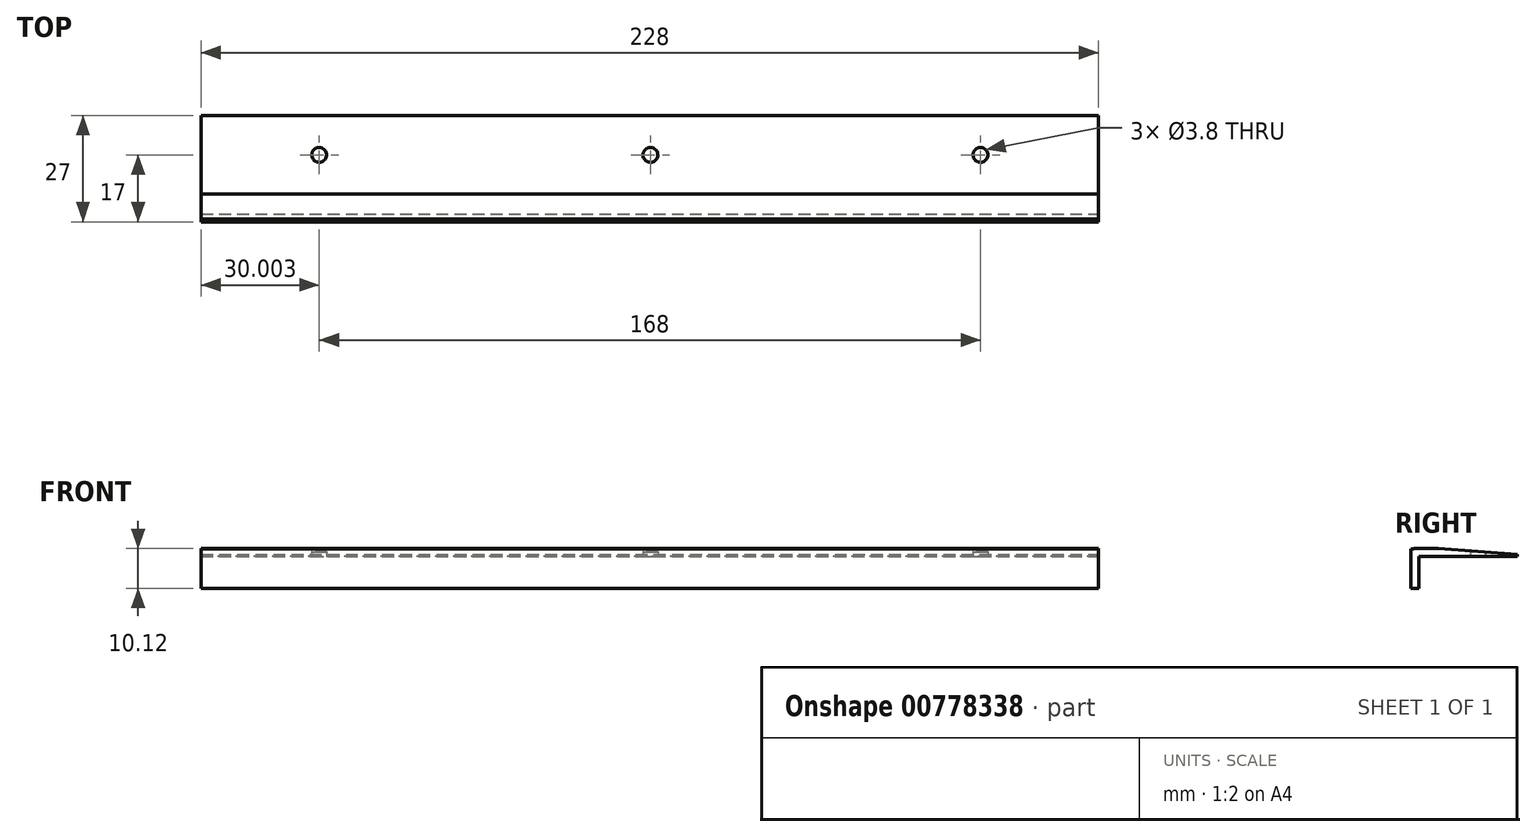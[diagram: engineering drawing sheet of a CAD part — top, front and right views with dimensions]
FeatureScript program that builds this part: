
annotation { "Feature Type Name" : "Feature", "Feature Type Description" : "" }
export const myFeature = defineFeature(function(context is Context, id is Id, definition is map)
    precondition{}
    {
        {
            var Q0;
            Q0=qCreatedBy(makeId("Front.planeOp"),FACE);
            var sketch = newSketch(context, id + "F0", { "sketchPlane" : qUnion([Q0])});
            skLineSegment(sketch, "E0.bottom", {"start": v(-110.8, 18.46) * mm, "end": v(117.2, 18.46) * mm});
            skLineSegment(sketch, "E0.top", {"start": v(-110.8, 8.46) * mm, "end": v(117.2, 8.46) * mm});
            skLineSegment(sketch, "E0.left", {"start": v(-110.8, 18.46) * mm, "end": v(-110.8, 8.46) * mm});
            skLineSegment(sketch, "E0.right", {"start": v(117.2, 18.46) * mm, "end": v(117.2, 8.46) * mm});
            skSolve(sketch);
        }
        {
            var Q0;
            Q0 = qSketchRegion(id + "F0", true);
            extrude(context, id + "F1", {"entities" : qUnion([Q0]), "depth" : 2 * mm, "offsetDistance" : 25 * mm});
        }
        {
            var Q0;
            Q0=qCreatedBy(makeId("Front.planeOp"),FACE);
            var sketch = newSketch(context, id + "F2", { "sketchPlane" : qUnion([Q0])});
            skLineSegment(sketch, "E1.bottom", {"start": v(117.21, 18.58) * mm, "end": v(-110.79, 18.58) * mm});
            skLineSegment(sketch, "E1.top", {"start": v(117.21, 16.58) * mm, "end": v(-110.79, 16.58) * mm});
            skLineSegment(sketch, "E1.left", {"start": v(117.21, 18.58) * mm, "end": v(117.21, 16.58) * mm});
            skLineSegment(sketch, "E1.right", {"start": v(-110.79, 18.58) * mm, "end": v(-110.79, 16.58) * mm});
            skSolve(sketch);
        }
        {
            var Q0;
            Q0 = qSketchRegion(id + "F2", true);
            extrude(context, id + "F3", {"entities" : qUnion([Q0]), "operationType" : NewBodyOperationType.ADD, "depth" : 1.3 * mm, "offsetDistance" : 25 * mm, "hasSecondDirection" : true, "secondDirectionOppositeDirection" : true, "secondDirectionDepth" : 25 * mm});
        }
        {
            var Q0;
            Q0=makeQuery(id+"F3.opExtrude","CAP_EDGE",EDGE,{"disambiguationData":[OSD([sQuery(id+"F2.wireOp",EDGE,"E1.bottom")])],"isStart":true});
            chamfer(context, id + "F4", {"entities" : qUnion([Q0]), "chamferType" : ChamferType.TWO_OFFSETS, "width1" : 20 * mm, "oppositeDirection" : false, "width2" : 1.5 * mm, "tangentPropagation" : true});
        }
        {
            var Q0;
            Q0=qCreatedBy(makeId("Top.planeOp"),FACE);
            var sketch = newSketch(context, id + "F5", { "sketchPlane" : qUnion([Q0])});
            skPoint(sketch, "E2", {"position": v(-80.79, 15) * mm});
            skPoint(sketch, "E3", {"position": v(87.21, 15) * mm});
            skPoint(sketch, "E4", {"position": v(0, 248.7) * mm});
            skPoint(sketch, "E5", {"position": v(3.36, 15) * mm});
            skSolve(sketch);
        }
        {
            var Q0;
            Q0=sQuery(id+"F5.wireOp",VERTEX,"E2");
            var Q1;
            Q1=sQuery(id+"F5.wireOp",VERTEX,"E5");
            var Q2;
            Q2=sQuery(id+"F5.wireOp",VERTEX,"E3");
            var Q3;
            Q3=makeQuery(id+"F1.opExtrude","SWEPT_BODY",BODY,{"disambiguationData":[OSD([sQuery(id+"F0.wireOp",EDGE,"E0.bottom"),sQuery(id+"F0.wireOp",EDGE,"E0.top"),sQuery(id+"F0.wireOp",EDGE,"E0.left"),sQuery(id+"F0.wireOp",EDGE,"E0.right")])]});
            hole(context, id + "F6", {"style" : HoleStyle.C_SINK, "endStyle" : HoleEndStyle.THROUGH, "oppositeDirection" : true, "standardTappedOrClearance" : lookupTablePath({ "standard" : "ANSI", "fit" : "Normal (ASME)", "size" : "#6", "type" : "Clearance" }), "standardBlindInLast" : lookupTablePath({ "fit" : "Free", "standard" : "ANSI", "size" : "#6", "type" : "Clearance" }), "holeDiameter" : 3.8 * mm, "cSinkDiameter" : 7.8 * mm, "cSinkAngle" : 82 * degree, "majorDiameter" : 5 * mm, "isTappedThrough" : true, "tappedDepth" : 12 * mm, "tapClearance" : 3, "startFromSketch" : true, "locations" : qUnion([Q0, Q1, Q2]), "scope" : qUnion([Q3])});
        }
    });
